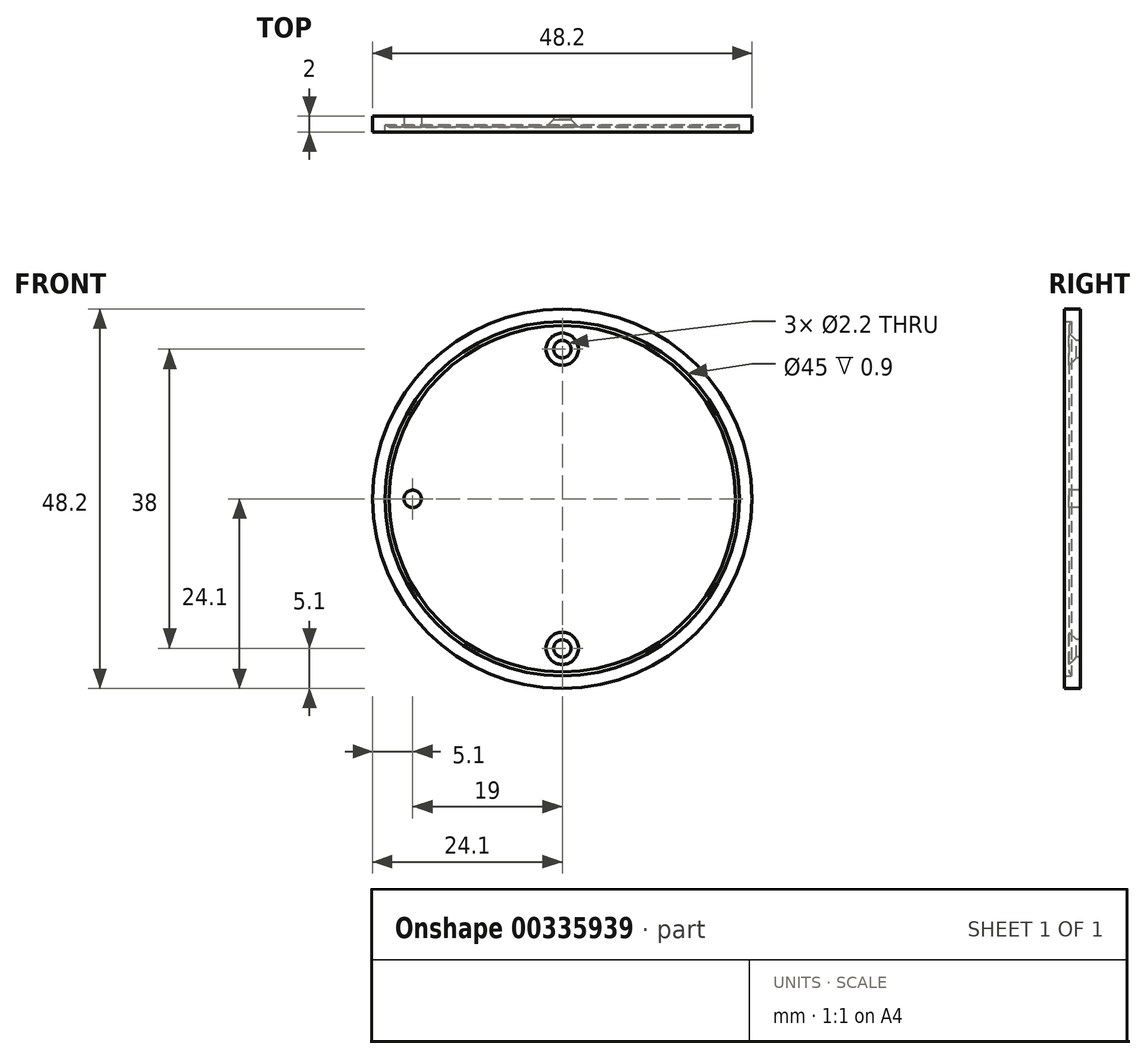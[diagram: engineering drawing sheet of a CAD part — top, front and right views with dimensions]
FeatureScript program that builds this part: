
annotation { "Feature Type Name" : "Feature", "Feature Type Description" : "" }
export const myFeature = defineFeature(function(context is Context, id is Id, definition is map)
    precondition{}
    {
        {
            var Q0;
            Q0=qCreatedBy(makeId("Right.planeOp"),FACE);
            var sketch = newSketch(context, id + "F0", { "sketchPlane" : qUnion([Q0])});
            skLineSegment(sketch, "E0", {"start": v(0, 0) * mm, "end": v(0, 21.98) * mm});
            skLineSegment(sketch, "E1", {"start": v(0, 21.98) * mm, "end": v(0.3, 22.5) * mm});
            skLineSegment(sketch, "E2", {"start": v(0.3, 22.5) * mm, "end": v(-0.6, 22.5) * mm});
            skLineSegment(sketch, "E3", {"start": v(-0.6, 22.5) * mm, "end": v(-0.6, 24.1) * mm});
            skLineSegment(sketch, "E4", {"start": v(-0.6, 24.1) * mm, "end": v(1.4, 24.1) * mm});
            skLineSegment(sketch, "E5", {"start": v(1.4, 24.1) * mm, "end": v(1.4, 0) * mm});
            skLineSegment(sketch, "E6", {"start": v(1.4, 0) * mm, "end": v(0, 0) * mm});
            skSolve(sketch);
        }
        {
            var Q0;
            Q0 = qSketchRegion(id + "F0", true);
            var Q1;
            Q1=sQuery(id+"F0.wireOp",EDGE,"E6");
            revolve(context, id + "F1", {"entities" : qUnion([Q0]), "axis" : qUnion([Q1]), "revolveType" : RevolveType.FULL});
        }
        {
            var Q0;
            Q0=makeQuery(id+"F1.opRevolve","SWEPT_FACE",FACE,{"disambiguationData":[OSD([sQuery(id+"F0.wireOp",EDGE,"E0")])]});
            var sketch = newSketch(context, id + "F2", { "sketchPlane" : qUnion([Q0])});
            skCircle(sketch, "E7", {"center": v(0, 0) * mm, "radius": 19 * mm, "construction": true});
            skPoint(sketch, "E8", {"position": v(0, 19) * mm});
            skPoint(sketch, "E9", {"position": v(-19, 0) * mm});
            skPoint(sketch, "E10", {"position": v(0, -19) * mm});
            skSolve(sketch);
        }
        {
            var Q0;
            Q0=sQuery(id+"F2.wireOp",VERTEX,"E9");
            var Q1;
            Q1=makeQuery(id+"F1.opRevolve","SWEPT_BODY",BODY,{"disambiguationData":[OSD([sQuery(id+"F0.wireOp",EDGE,"E0"),sQuery(id+"F0.wireOp",EDGE,"E1"),sQuery(id+"F0.wireOp",EDGE,"E2"),sQuery(id+"F0.wireOp",EDGE,"E3"),sQuery(id+"F0.wireOp",EDGE,"E4"),sQuery(id+"F0.wireOp",EDGE,"E5"),sQuery(id+"F0.wireOp",EDGE,"E6")])]});
            hole(context, id + "F3", {"style" : HoleStyle.SIMPLE, "endStyle" : HoleEndStyle.THROUGH, "holeDiameter" : 2.2 * mm, "tappedDepth" : 12 * mm, "tapClearance" : 3, "locations" : qUnion([Q0]), "scope" : qUnion([Q1])});
        }
        {
            var Q0;
            Q0=sQuery(id+"F2.wireOp",VERTEX,"E8");
            var Q1;
            Q1=sQuery(id+"F2.wireOp",VERTEX,"E10");
            var Q2;
            Q2=makeQuery(id+"F1.opRevolve","SWEPT_BODY",BODY,{"disambiguationData":[OSD([sQuery(id+"F0.wireOp",EDGE,"E0"),sQuery(id+"F0.wireOp",EDGE,"E1"),sQuery(id+"F0.wireOp",EDGE,"E2"),sQuery(id+"F0.wireOp",EDGE,"E3"),sQuery(id+"F0.wireOp",EDGE,"E4"),sQuery(id+"F0.wireOp",EDGE,"E5"),sQuery(id+"F0.wireOp",EDGE,"E6")])]});
            hole(context, id + "F4", {"style" : HoleStyle.C_SINK, "endStyle" : HoleEndStyle.THROUGH, "holeDiameter" : 2.2 * mm, "cSinkDiameter" : 4.1 * mm, "cSinkAngle" : 90 * degree, "tappedDepth" : 12 * mm, "tapClearance" : 3, "locations" : qUnion([Q0, Q1]), "scope" : qUnion([Q2])});
        }
    });
